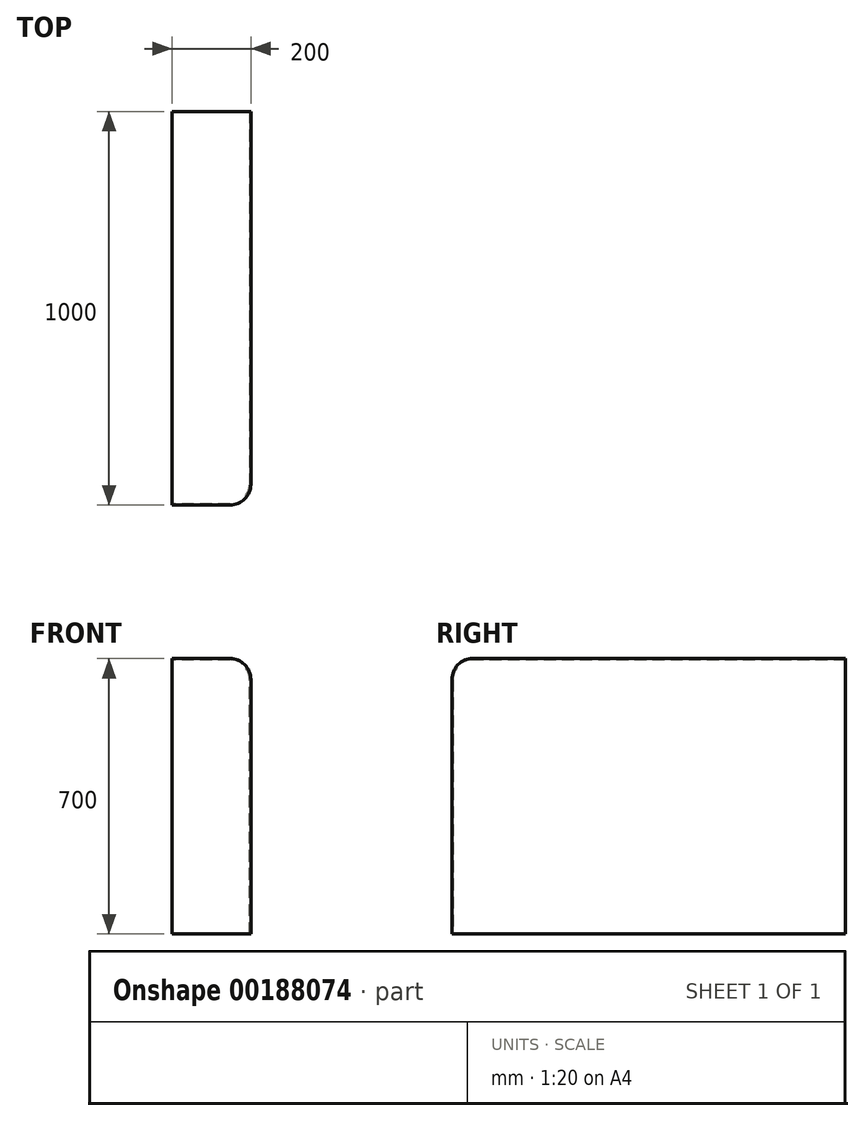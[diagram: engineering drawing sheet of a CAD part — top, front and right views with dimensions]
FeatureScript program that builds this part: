
annotation { "Feature Type Name" : "Feature", "Feature Type Description" : "" }
export const myFeature = defineFeature(function(context is Context, id is Id, definition is map)
    precondition{}
    {
        {
            var Q0;
            Q0=qCreatedBy(makeId("Right.planeOp"),FACE);
            var sketch = newSketch(context, id + "F0", { "sketchPlane" : qUnion([Q0])});
            skLineSegment(sketch, "E0.bottom", {"start": v(500, -350) * mm, "end": v(-500, -350) * mm});
            skLineSegment(sketch, "E0.top", {"start": v(500, 350) * mm, "end": v(-500, 350) * mm});
            skLineSegment(sketch, "E0.left", {"start": v(500, -350) * mm, "end": v(500, 350) * mm});
            skLineSegment(sketch, "E0.right", {"start": v(-500, -350) * mm, "end": v(-500, 350) * mm});
            skPoint(sketch, "E0.middle", {"position": v(0, 0) * mm});
            skSolve(sketch);
        }
        {
            var Q0;
            Q0=qSketchRegion(id+"F0",true);
            extrude(context, id + "F1", {"entities" : qUnion([Q0]), "depth" : 200 * mm});
        }
        {
            var Q0;
            Q0=makeQuery(id+"F1.opExtrude","CAP_FACE",FACE,{"disambiguationData":[OSD([sQuery(id+"F0.wireOp",EDGE,"E0.bottom"),sQuery(id+"F0.wireOp",EDGE,"E0.top"),sQuery(id+"F0.wireOp",EDGE,"E0.left"),sQuery(id+"F0.wireOp",EDGE,"E0.right")])],"isStart":true});
            var sketch = newSketch(context, id + "F2", { "sketchPlane" : qUnion([Q0])});
            skLineSegment(sketch, "E1.bottom", {"start": v(-500, 347) * mm, "end": v(497, 347) * mm});
            skLineSegment(sketch, "E1.top", {"start": v(-500, -350) * mm, "end": v(497, -350) * mm});
            skLineSegment(sketch, "E1.left", {"start": v(-500, 347) * mm, "end": v(-500, -350) * mm});
            skLineSegment(sketch, "E1.right", {"start": v(497, 347) * mm, "end": v(497, -350) * mm});
            skSolve(sketch);
        }
        {
            var Q0;
            Q0 = qSketchRegion(id + "F2", true);
            extrude(context, id + "F3", {"entities" : qUnion([Q0]), "operationType" : NewBodyOperationType.REMOVE, "oppositeDirection" : true, "depth" : 197 * mm});
        }
        {
            var Q0;
            Q0=makeQuery(id+"F3.boolean.opBoolean","COPY",EDGE,{"derivedFrom":makeQuery(id+"F3.opExtrude","CAP_EDGE",EDGE,{"disambiguationData":[OSD([sQuery(id+"F2.wireOp",EDGE,"E1.bottom")])],"isStart":false})});
            fillet(context, id + "F4", {"entities" : qUnion([Q0]), "radius" : 50 * mm, "tangentPropagation" : true, "allowEdgeOverflow" : false});
        }
        {
            var Q0;
            Q0=makeQuery(id+"F3.boolean.opBoolean","COPY",EDGE,{"derivedFrom":makeQuery(id+"F3.opExtrude","CAP_EDGE",EDGE,{"disambiguationData":[OSD([sQuery(id+"F2.wireOp",EDGE,"E1.right")])],"isStart":false})});
            fillet(context, id + "F5", {"entities" : qUnion([Q0]), "radius" : 50 * mm, "tangentPropagation" : true, "allowEdgeOverflow" : false});
        }
        {
            var Q0;
            Q0=makeQuery(id+"F1.opExtrude","CAP_EDGE",EDGE,{"disambiguationData":[OSD([sQuery(id+"F0.wireOp",EDGE,"E0.top")])],"isStart":false});
            fillet(context, id + "F6", {"entities" : qUnion([Q0]), "radius" : 53 * mm, "tangentPropagation" : true, "allowEdgeOverflow" : false});
        }
        {
            var Q0;
            Q0=makeQuery(id+"F1.opExtrude","CAP_EDGE",EDGE,{"disambiguationData":[OSD([sQuery(id+"F0.wireOp",EDGE,"E0.right")])],"isStart":false});
            fillet(context, id + "F7", {"entities" : qUnion([Q0]), "radius" : 53 * mm, "tangentPropagation" : true, "allowEdgeOverflow" : false});
        }
    });
